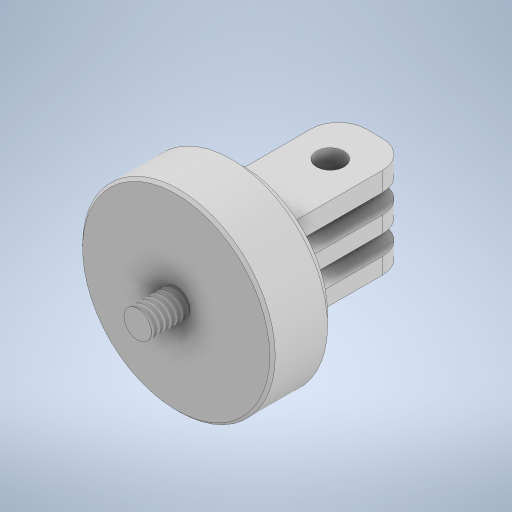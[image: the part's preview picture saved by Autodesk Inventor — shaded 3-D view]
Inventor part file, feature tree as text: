
AUTODESK INVENTOR PART (.ipt)
format: ipt  version: 2023.5 (Build 275446000, 446)  size: 369,152 bytes
history: native  units: in
note: dims shown in document units (in); Inventor stores cm internally (conversion verified against a paired STEP export)
features: fillet x18, extrude x6, sketch x5, chamfer x2, thread x1
ambient origin geometry x8: Origin, YZ Plane, XZ Plane, XY Plane, X Axis, Y Axis, Z Axis, Center Point
bodies: Solid1 (feature_tree)
feature tree (32):
  extrude  "Extrusion1"  Depth=0.4724in TaperAngle=0.0deg
  chamfer  "Chamfer1"  Distance=0.0197in Angle=45.0deg
  chamfer  "Chamfer2"  Distance=0.0787in Angle=45.0deg
  extrude  "Extrusion3"  Depth=0.5118in
  extrude  "Extrusion4"  Depth=0.1378in
  extrude  "Extrusion5"  Depth=0.9449in TaperAngle=0.0deg
  fillet  "Fillet1"  Radius=0.1378in
  fillet  "Fillet2"  Radius=0.1378in
  fillet  "Fillet3"  Radius=0.9449in
  fillet  "Fillet4"  Radius=0.1969in
  fillet  "Fillet5"  Radius=0.1969in
  fillet  "Fillet6"  Radius=0.1969in
  extrude  "Extrusion6"  Depth=0.1969in
  fillet  "Face Fillet1"
  fillet  "Face Fillet2"
  fillet  "Face Fillet3"
  fillet  "Face Fillet4"
  fillet  "Face Fillet5"
  fillet  "Face Fillet6"
  fillet  "Face Fillet7"
  fillet  "Face Fillet8"
  fillet  "Face Fillet9"
  fillet  "Face Fillet10"
  fillet  "Face Fillet11"
  fillet  "Face Fillet12"
  extrude  "Extrusion8"  Depth=0.1969in
  thread  "Thread3"  [1 undecoded]
  sketch  "Sketch5"  dims[d0=0.689in d1=0.4724in d2=0.0in d6=0.0197in d7=0.125in d8=45.0deg d9=0.0787in d10=0.125in d11=45.0deg]
  sketch  "Sketch6"  dims[d21=0.1181in d22=0.5118in]
  sketch  "Sketch7"  dims[d23=0.9449in d24=0.0in d25=0.1378in]
  sketch  "Sketch8"  dims[d26=0.1181in d27=0.9449in d28=0.0in d29=0.1378in d30=0.1378in d31=0.9449in d32=0.0in d33=0.1969in d34=0.1969in d35=0.1969in]
  sketch  "Sketch11"  dims[d36=0.1969in d37=0.1969in d38=0.1969in d41=0.9449in d42=0.0in d43=0.0591in d44=0.059in d45=0.059in d46=0.059in d47=0.059in d48=0.059in d49=0.059in d50=0.059in d51=0.059in d52=0.059in d53=0.059in d54=0.059in d60=0.1969in d61=0.2756in d62=0.0in d63=0.197in d64=0.0in d55=0.5in d56=0.0344in d57=0.5in d58=0.0344in]
note: 1 required parameter value undecoded (feature->parameter linkage not recoverable at this tier; creation-order binding heuristic only, values carry confidence <= 0.55)
